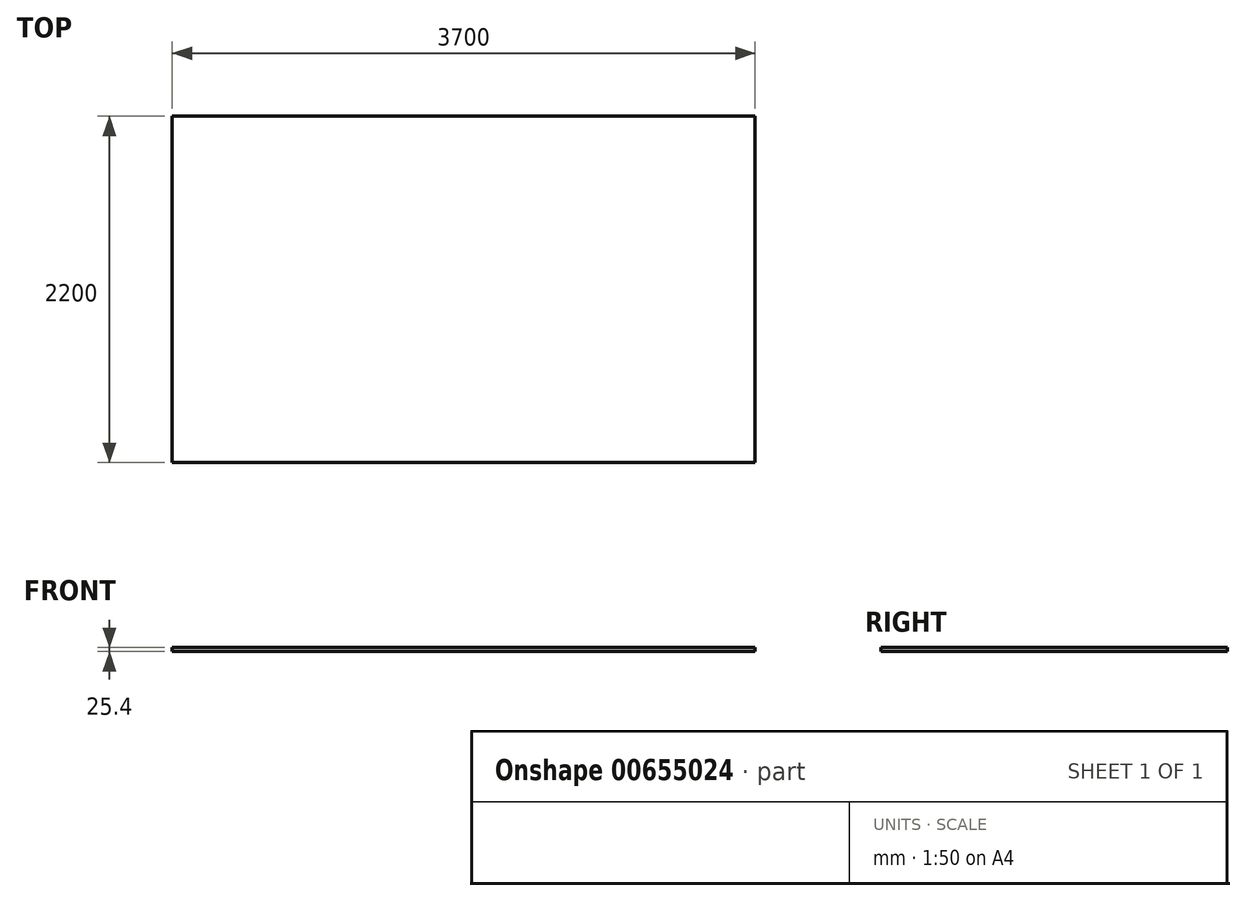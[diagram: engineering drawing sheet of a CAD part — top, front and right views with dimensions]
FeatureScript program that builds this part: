
annotation { "Feature Type Name" : "Feature", "Feature Type Description" : "" }
export const myFeature = defineFeature(function(context is Context, id is Id, definition is map)
    precondition{}
    {
        {
            var Q0;
            Q0=qCreatedBy(makeId("Top.planeOp"),FACE);
            var sketch = newSketch(context, id + "F0", { "sketchPlane" : qUnion([Q0])});
            skLineSegment(sketch, "E0.bottom", {"start": v(1850, -1100) * mm, "end": v(-1850, -1100) * mm});
            skLineSegment(sketch, "E0.top", {"start": v(1850, 1100) * mm, "end": v(-1850, 1100) * mm});
            skLineSegment(sketch, "E0.left", {"start": v(1850, -1100) * mm, "end": v(1850, 1100) * mm});
            skLineSegment(sketch, "E0.right", {"start": v(-1850, -1100) * mm, "end": v(-1850, 1100) * mm});
            skPoint(sketch, "E0.middle", {"position": v(0, 0) * mm});
            skSolve(sketch);
        }
        {
            var Q0;
            Q0=makeQuery(id+"F0.imprint","IMPRINT",FACE,{"disambiguationData":[TD([[makeQuery(id+"F0.imprint","IMPRINT",EDGE,{"derivedFrom":sQuery(id+"F0.wireOp",EDGE,"E0.bottom")}),-1.0]])]});
            extrude(context, id + "F1", {"entities" : qUnion([Q0]), "depth" : 25.4 * mm, "offsetDistance" : 25.4 * mm});
        }
    });
